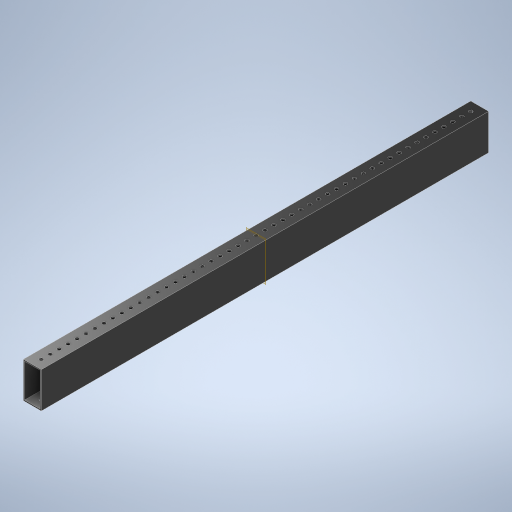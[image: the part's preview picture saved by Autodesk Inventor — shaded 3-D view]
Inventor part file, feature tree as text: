
AUTODESK INVENTOR PART (.ipt)
format: ipt  version: 2024.2 (Build 282272000, 272)  size: 809,984 bytes
history: native  units: in
note: dims shown in document units (in); Inventor stores cm internally (conversion verified against a paired STEP export)
features: other x13, extrude x10, hole x3, pattern_linear x3, mirror x3, plane x2, sheet_metal_op x1, sketch x1
ambient origin geometry x8: Origin, YZ Plane, XZ Plane, XY Plane, X Axis, Y Axis, Z Axis, Center Point
bodies: Solid1 (feature_tree)
feature tree (36):
  other  "Blocks"
  other  "Base Sketch"
  extrude  "Base"  Depth=1.0in
  extrude  "MAX Corner"  Depth=0.0625in
  extrude  "MAX Corner Cut"  Depth=0.0625in
  extrude  "Scribe Lines"  Depth=1.0in
  other  "Side Middle"
  other  "Top Middle"
  other  "Side Holes Sketch"
  hole  "Top Side Hole"  [1 undecoded]
  hole  "Mid Side Hole"  [1 undecoded]
  hole  "Btm Side Hole"  [1 undecoded]
  pattern_linear  "Side Holes"  Spacing1=0.04in  [1 undecoded]
  mirror  "Side Mirror"
  extrude  "MAXTube Hole"  Depth=25.0in
  extrude  "MAXTube Outside"  TaperAngle=0.0deg  [1 undecoded]
  pattern_linear  "MAXTube Pattern"  Spacing1=25.0in  [1 undecoded]
  mirror  "MAXTube Mirror"
  extrude  "Left Top Hole"  TaperAngle=0.0deg  [1 undecoded]
  extrude  "Mid Top Hole"  TaperAngle=0.0deg  [1 undecoded]
  extrude  "Right Top Hole"  Depth=1.0in
  pattern_linear  "Top Holes"  Spacing1=0.0in  [1 undecoded]
  mirror  "Top Mirror"
  extrude  "Extrusion11"  Depth=1.0in
  plane  "Work Plane5"
  sheet_metal_op  "Corner"
  other  "MAXTube"
  plane  "Work Plane3"
  sketch  "Sketch5"  dims[d0=2.0in d1=1.0in d2=0.0625in d3=0.0625in d4=0.4375in d5=0.04in d6=0.0671in d7=0.0272in d8=0.0in d9=0.0in d10=0.0in d11=0.085in d12=0.085in d16=0.04in d17=0.04in d18=0.04in d19=0.04in d20=25.0in d21=0.0in d22=25.0in d23=0.0in d24=0.0in d25=0.0in d26=0.005in d30=0.0in d31=0.0in d34=0.5in d35=0.5in d38=0.5in d40=0.196in d41=0.75in d42=0.375in d43=0.25in d44=0.5635in d45=1.0in d46=0.8108in d47=0.196in d48=0.75in d49=0.375in d50=0.25in d51=0.5635in d52=1.0in d53=0.8108in d54=0.196in d55=0.75in d56=0.375in d57=0.25in d58=0.5635in d59=1.0in d60=0.8108in d61=0.5in d62=0.3937in d64=2.0in d69=1.5in d70=0.0in d71=0.0in d72=2.7559in d74=2.0in d78=2.0in d79=-12.5in d80=0.196in d81=0.0in d82=0.0in d83=0.5in d84=0.0in d85=0.0in d86=0.0in d87=0.0in d88=0.0in d89=0.0in d90=9.8425in d92=0.5in d93=1.0in d95=0.0in d96=0.0in d97=1.5in d98=22.0in d100=-12.5in d101=0.25in d102=0.25in d103=0.25in d104=0.25in d105=0.5in d106=0.0in]
  other  "Corner:5"
  other  "Corner:6"
  other  "Corner:7"
  other  "Corner:8"
  other  "MAXTube:1"
  other  "MAXTube:2"
  other  "MAXTube:3"
note: 9 required parameter values undecoded (feature->parameter linkage not recoverable at this tier; creation-order binding heuristic only, values carry confidence <= 0.55)
